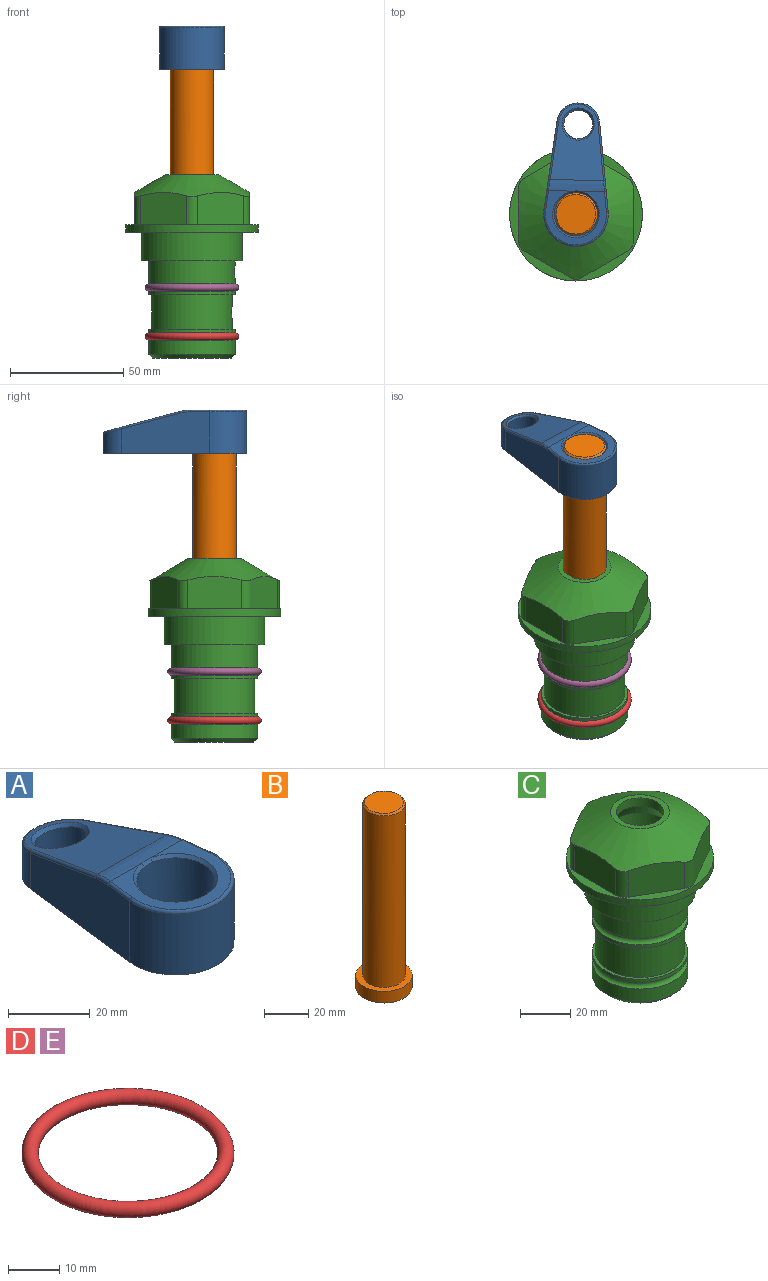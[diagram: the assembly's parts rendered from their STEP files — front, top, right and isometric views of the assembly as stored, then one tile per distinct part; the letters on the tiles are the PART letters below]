
ASSEMBLY  parts=5 mates=4
PART A: 31 faces, bbox 31.7x65.5x19.8 mm
  f0: plane 39.12x18.26mm, normal (0.99,0.12,0), area 612.2mm2, adj f1,f4,f7,f11,f13,f15
  f1: cylinder r=9.53mm len=18.91mm, axis (0,0,-1), area 296.1mm2, adj f0,f2,f7,f17
  f2: plane 39.12x18.26mm, normal (-0.99,0.12,0), area 612.2mm2, adj f1,f4,f7,f12,f14,f16
  f3: cylinder r=6.35mm len=12.7mm, axis (0,0,-1), area 362.4mm2, adj f7,f18
  f4: cylinder r=14.29mm len=28.58mm, axis (0,0,-1), area 882.2mm2, adj f0,f2,f7,f10
  f5: cylinder r=9.53mm len=19.05mm, axis (0,0,-1), area 1092.6mm2, adj f7,f19,f20
  f6: plane 26.99x23.69mm, normal (0,0,1), area 216.2mm2, adj f9,f10,f11,f12,f19
  f7: plane 63.5x28.58mm, normal (0,0,-1), area 661.8mm2, adj f0,f1,f2,f3,f4,f5,f22,f23
  f8: plane 33.52x23.6mm, normal (0,0.26,0.97), area 486mm2, adj f9,f15,f16,f17,f18
  f9: cylinder r=19.05mm len=24.72mm, axis (1,0,0), area 120.4mm2, adj f6,f8,f13,f14,f20
  f10: torus R=13.49mm, axis (0,0,1), area 59mm2, adj f4,f6,f11,f12
  f11: cylinder r=0.79mm len=8.67mm, axis (0.12,-0.99,0), area 10.8mm2, adj f0,f6,f10,f13
  f12: cylinder r=0.79mm len=8.67mm, axis (0.12,0.99,0), area 10.8mm2, adj f2,f6,f10,f14
  f13: bspline ~4.95x1.42mm, area 6.1mm2, adj f0,f9,f11,f15
  f14: bspline ~4.95x1.42mm, area 6.1mm2, adj f2,f9,f12,f16
  f15: cylinder r=0.79mm len=25.95mm, axis (0.12,-0.96,0.26), area 32.9mm2, adj f0,f8,f13,f17
  f16: cylinder r=0.79mm len=25.95mm, axis (0.12,0.96,-0.26), area 32.9mm2, adj f2,f8,f14,f17
  f17: bspline ~18.91x8.38mm, area 30mm2, adj f1,f8,f15,f16
  f18: bspline ~14.29x14.29mm, area 48.3mm2, adj f3,f8
  f19: cone r=9.53mm half-angle=45deg, axis (0,0,1), area 66.5mm2, adj f5,f6,f20
  f20: bspline ~3.22x0.96mm, area 3.5mm2, adj f5,f9,f19
  f21: plane 2.75x2.72mm, normal (0,0,-1), area 2.9mm2, adj f23,f25,f28
  f22: plane 23.05x15.88mm, normal (-0.99,-0.12,0), area 323.6mm2, adj f7,f25,f26,f27,f28,f29
  f23: plane 23.05x15.88mm, normal (0.99,-0.12,0), area 323.6mm2, adj f7,f21,f25,f27,f28,f30
  f24: cylinder r=9.53mm len=10.69mm, axis (0,0,-1), area 114.7mm2, adj f7,f27,f29,f30
  f25: cylinder r=12.7mm len=20.59mm, axis (0,0,-1), area 381.1mm2, adj f7,f21,f22,f23,f26,f28
  f26: plane 2.75x2.72mm, normal (0,0,-1), area 2.9mm2, adj f22,f25,f28
  f27: plane 19.72x18.37mm, normal (0,-0.26,-0.97), area 291.8mm2, adj f22,f23,f24,f28,f29,f30
  f28: cylinder r=15.88mm len=19.92mm, axis (1,0,0), area 54.8mm2, adj f21,f22,f23,f25,f26,f27
  f29: cylinder r=1.59mm len=11mm, axis (0,0,-1), area 34.7mm2, adj f7,f22,f24,f27
  f30: cylinder r=1.59mm len=11mm, axis (0,0,-1), area 34.7mm2, adj f7,f23,f24,f27
PART B: 6 faces, bbox 25.4x25.4x101.6 mm
  f0: plane 17.46x17.46mm, normal (0,0,1), area 239.5mm2, adj f5
  f1: plane 25.4x25.4mm, normal (0,0,-1), area 506.7mm2, adj f2
  f2: cylinder r=12.7mm len=25.4mm, axis (0,0,1), area 506.7mm2, adj f1,f3
  f3: plane 25.4x25.4mm, normal (0,0,1), area 221.7mm2, adj f2,f4
  f4: cylinder r=9.53mm len=94.46mm, axis (0,0,1), area 5653mm2, adj f3,f5
  f5: cone r=8.73mm half-angle=45deg, axis (0,0,-1), area 64.4mm2, adj f0,f4
PART C: 36 faces, bbox 58.7x58.7x81 mm
  f0: cylinder r=17.78mm len=35.56mm, axis (0,0,1), area 1670.8mm2, adj f23,f24,f31
  f1: cylinder r=19.05mm len=38.1mm, axis (0,0,1), area 1191.9mm2, adj f26,f27,f30
  f2: plane 58.66x58.66mm, normal (0,0,-1), area 1150.6mm2, adj f3,f28
  f3: cylinder r=29.33mm len=58.66mm, axis (0,0,-1), area 585.1mm2, adj f2,f4
  f4: plane 58.66x58.66mm, normal (0,0,1), area 475.9mm2, adj f3,f5,f6,f7,f8,f9,f10,f11
  f5: plane 20.32x14.34mm, normal (-0.5,0.87,0), area 324.4mm2, adj f4,f15,f16,f17
  f6: plane 20.32x14.34mm, normal (0.5,0.87,0), area 324.4mm2, adj f4,f14,f15,f17
  f7: plane 23.48x14.34mm, normal (1,0,0), area 324.4mm2, adj f4,f13,f14,f17
  f8: plane 20.32x14.34mm, normal (0.5,-0.87,0), area 324.4mm2, adj f4,f12,f13,f17
  f9: plane 20.32x14.34mm, normal (-0.5,-0.87,0), area 324.4mm2, adj f4,f11,f12,f17
  f10: plane 23.48x14.34mm, normal (-1,0,0), area 324.4mm2, adj f4,f11,f16,f17
  f11: cylinder r=5.08mm len=12.85mm, axis (0,0,-1), area 67.2mm2, adj f4,f9,f10,f17
  f12: cylinder r=5.08mm len=12.85mm, axis (0,0,-1), area 67.2mm2, adj f4,f8,f9,f17
  f13: cylinder r=5.08mm len=12.85mm, axis (0,0,-1), area 67.2mm2, adj f4,f7,f8,f17
  f14: cylinder r=5.08mm len=12.85mm, axis (0,0,-1), area 67.2mm2, adj f4,f6,f7,f17
  f15: cylinder r=5.08mm len=12.85mm, axis (0,0,-1), area 67.2mm2, adj f4,f5,f6,f17
  f16: cylinder r=5.08mm len=12.85mm, axis (0,0,-1), area 67.2mm2, adj f4,f5,f10,f17
  f17: cone r=11.73mm half-angle=60deg, axis (0,0,-1), area 2071.8mm2, adj f5,f6,f7,f8,f9,f10,f11,f12
  f18: plane 23.46x23.46mm, normal (0,0,1), area 147.4mm2, adj f17,f35
  f19: plane 34.93x34.93mm, normal (0,0,-1), area 958mm2, adj f29
  f20: cylinder r=19.05mm len=38.1mm, axis (0,0,1), area 760.1mm2, adj f21,f29
  f21: torus R=19.05mm, axis (0,0,1), area 565.3mm2, adj f20,f22
  f22: cylinder r=19.05mm len=38.1mm, axis (0,0,1), area 190mm2, adj f21,f23
  f23: plane 38.1x38.1mm, normal (0,0,1), area 146.9mm2, adj f0,f22
  f24: plane 38.1x38.1mm, normal (0,0,-1), area 146.9mm2, adj f0,f25
  f25: cylinder r=19.05mm len=38.1mm, axis (0,0,1), area 190mm2, adj f24,f26
  f26: torus R=19.05mm, axis (0,0,1), area 565.3mm2, adj f1,f25
  f27: plane 44.45x44.45mm, normal (0,0,-1), area 411.7mm2, adj f1,f28
  f28: cylinder r=22.23mm len=44.45mm, axis (0,0,1), area 1773.5mm2, adj f2,f27
  f29: cone r=19.05mm half-angle=45deg, axis (0,0,1), area 257.5mm2, adj f19,f20
  f30: cylinder r=3.17mm len=6.75mm, axis (-1,0,0), area 128mm2, adj f1,f33
  f31: cylinder r=3.17mm len=6.35mm, axis (-1,0,0), area 102.5mm2, adj f0,f33
  f32: plane 25.4x25.4mm, normal (0,0,1), area 506.7mm2, adj f33
  f33: cylinder r=12.7mm len=66.42mm, axis (0,0,-1), area 5236.2mm2, adj f30,f31,f32,f34
  f34: cone r=9.53mm half-angle=30deg, axis (0,0,-1), area 443.4mm2, adj f33,f35
  f35: cylinder r=9.53mm len=19.05mm, axis (0,0,-1), area 240.9mm2, adj f18,f34
PART D: 1 faces, bbox 44.7x44.7x3.2 mm
  f0: torus R=19.05mm, axis (0,0,1), area 1193.9mm2
PART E: same geometry as D
PLACE A rot(axis=(0,0,-1),1.4deg) t=(0,0,27.55)mm
PLACE B rot(axis=(0,0,-1),1.4deg) t=(0,0,27.55)mm
PLACE C at identity fixed
PLACE D t=(0,0,-21.59)mm
PLACE E at identity
MATE cylindrical B.f2 <-> C.f0  axis (0,0,-1) through (0,0,-10.55)mm
MATE fastened D.f0 <-> C.f0  axis (0,0,1) through (0,0,-46.1)mm
MATE fastened E.f0 <-> C.f0  axis (0,0,1) through (0,0,-24.51)mm
MATE fastened A.f4 <-> B.f2  axis (0,0,-1) through (0,0,90.26)mm
